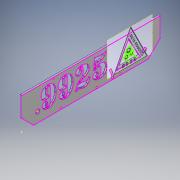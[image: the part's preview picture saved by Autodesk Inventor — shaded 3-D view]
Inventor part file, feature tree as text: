
AUTODESK INVENTOR PART (.ipt)
format: ipt  version: 2019 (Build 230136000, 136)  size: 1,334,784 bytes
history: native  units: in
note: dims shown in document units (in); Inventor stores cm internally (conversion verified against a paired STEP export)
features: sketch x6, extrude x4, projected_geometry x3, chamfer x2, hole x2, other x1
ambient origin geometry x8: Origin, YZ Plane, XZ Plane, XY Plane, X Axis, Y Axis, Z Axis, Center Point
bodies: Solid1 (feature_tree)
feature tree (18):
  extrude  "Extrusion1"  Depth=17.5in
  chamfer  "Chamfer1"  Distance=0.1875in
  chamfer  "Chamfer2"  Distance=1.5in Angle=45.0deg
  hole  "Hole3"  [1 undecoded]
  sketch  "Sketch9"  dims[d3=1.25in]
  hole  "Hole4"  [1 undecoded]
  extrude  "Extrusion6"  Depth=0.603in
  extrude  "Extrusion7"  Depth=0.125in
  extrude  "Extrusion8"  Depth=0.63in
  sketch  "Sketch13"  dims[d11=1.5in d12=0.125in d13=45.0deg d22=6.517in d23=0.125in d24=0.603in d25=0.125in d26=0.63in d27=6.517in d28=0.125in d29=0.603in d30=6.517in d31=0.125in d32=0.63in d33=6.517in d110=0.175in d111=0.175in d112=4.0in d113=4.0in d114=0.175in d115=0.175in d116=0.15in d117=0.75in d118=0.375in d119=0.25in d120=0.5635in d121=1.0in d122=0.8108in d123=5.0in d124=5.0in d125=8.0in d126=0.15in d127=0.2in d128=0.75in d129=0.375in d130=0.25in d131=0.5635in d132=1.0in d133=0.8108in d134=2.0in d135=0.2in d137=1.0in d138=0.0in d139=0.2in d140=1.0in d141=1.0in d142=0.0in d143=0.75in d144=0.75in d145=0.6033in d146=4.0in d147=0.0in d148=0.0in]
  sketch  "Sketch1"  dims[d0=4.0in d1=17.5in]
  sketch  "Sketch8"  dims[d2=0.501in]
  projected_geometry  "Projected Loop7"
  sketch  "Sketch10"  dims[d4=2.0in]
  sketch  "Sketch11"  dims[d5=2.0in d6=0.1875in d7=0.0in d8=1.5in d9=0.125in d10=45.0deg]
  other  "Image1"
  projected_geometry  "Projected Loop8"
  projected_geometry  "Projected Loop9"
note: 2 required parameter values undecoded (feature->parameter linkage not recoverable at this tier; creation-order binding heuristic only, values carry confidence <= 0.55)
